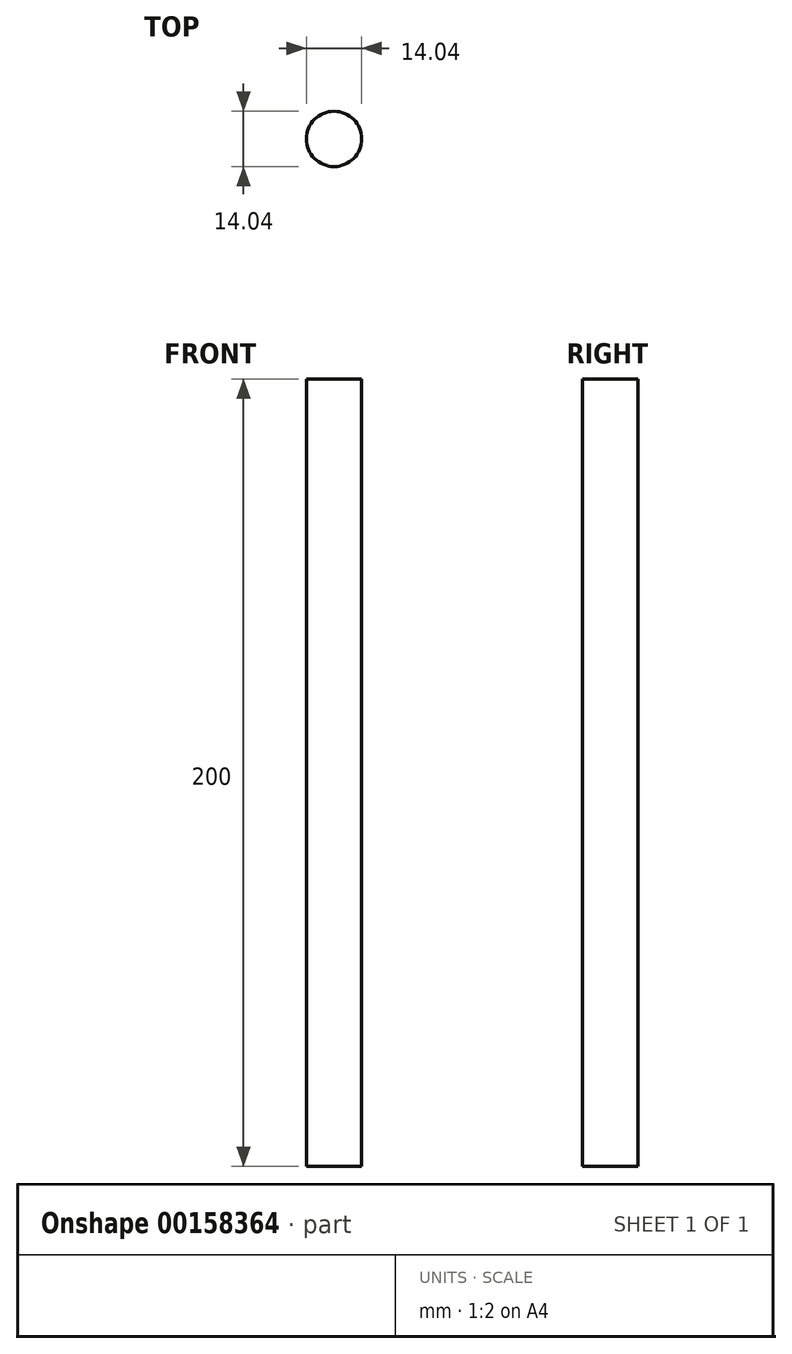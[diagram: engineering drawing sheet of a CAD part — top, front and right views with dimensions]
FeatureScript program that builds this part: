
annotation { "Feature Type Name" : "Feature", "Feature Type Description" : "" }
export const myFeature = defineFeature(function(context is Context, id is Id, definition is map)
    precondition{}
    {
        {
            var Q0;
            Q0=qCreatedBy(makeId("Top.planeOp"),FACE);
            var sketch = newSketch(context, id + "F0", { "sketchPlane" : qUnion([Q0])});
            skCircle(sketch, "E0", {"center": v(0, 0) * mm, "radius": 7.02 * mm});
            skSolve(sketch);
        }
        {
            var Q0;
            Q0 = qSketchRegion(id + "F0", true);
            var Q1;
            Q1=makeQuery(id+"F0.imprint","IMPRINT",FACE,{"disambiguationData":[TD([[makeQuery(id+"F0.imprint","IMPRINT",EDGE,{"derivedFrom":sQuery(id+"F0.wireOp",EDGE,"E0")}),1.0]])]});
            extrude(context, id + "F1", {"entities" : qUnion([Q0, Q1]), "depth" : 200 * mm});
        }
    });
